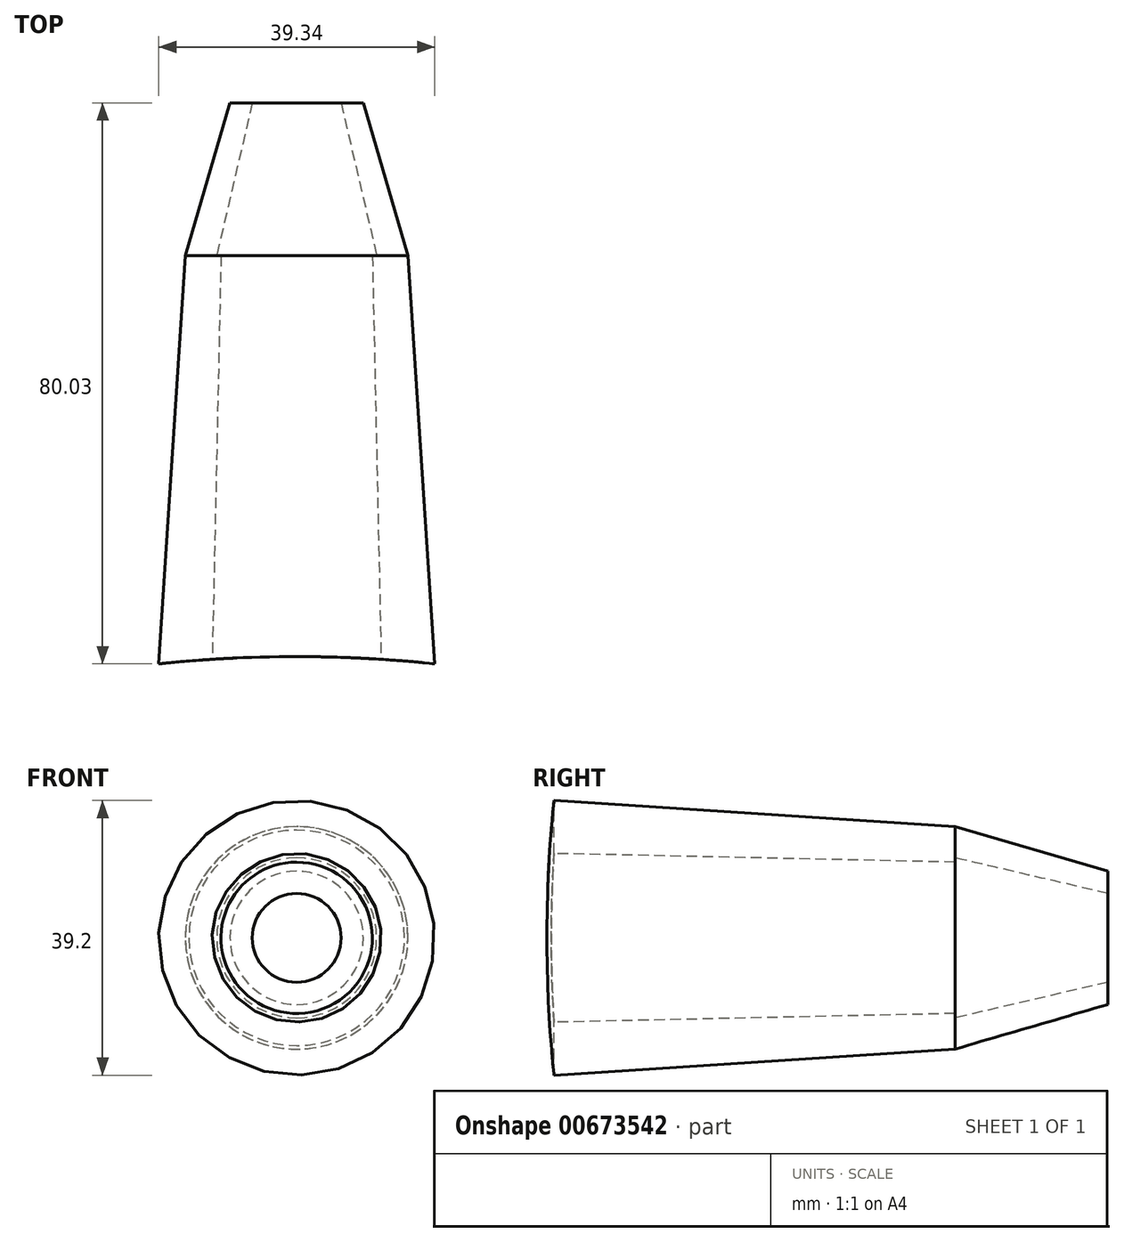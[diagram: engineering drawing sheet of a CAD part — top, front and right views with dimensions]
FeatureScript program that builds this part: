
annotation { "Feature Type Name" : "Feature", "Feature Type Description" : "" }
export const myFeature = defineFeature(function(context is Context, id is Id, definition is map)
    precondition{}
    {
        {
            var Q0;
            Q0=qCreatedBy(makeId("Top.planeOp"),FACE);
            var sketch = newSketch(context, id + "F0", { "sketchPlane" : qUnion([Q0])});
            skLineSegment(sketch, "E0", {"start": v(0, 0) * mm, "end": v(-19.69, 0) * mm});
            skLineSegment(sketch, "E1", {"start": v(-19.69, 0) * mm, "end": v(-15.88, 58.42) * mm});
            skLineSegment(sketch, "E2", {"start": v(-15.88, 58.42) * mm, "end": v(0, 58.42) * mm});
            skLineSegment(sketch, "E3", {"start": v(0, 58.42) * mm, "end": v(0, 0) * mm});
            skLineSegment(sketch, "E4", {"start": v(-10.8, 58.42) * mm, "end": v(-12.06, 0) * mm});
            skSolve(sketch);
        }
        {
            var Q0;
            {var subQ0=sQuery(id+"F0.wireOp",EDGE,"E1");Q0=makeQuery(id+"F0.imprint","IMPRINT",FACE,{"disambiguationData":[TD([[makeQuery(id+"F0.imprint","IMPRINT",EDGE,{"derivedFrom":subQ0}),-1.0]])]});}
            var Q1;
            Q1=sQuery(id+"F0.wireOp",EDGE,"E3");
            revolve(context, id + "F1", {"entities" : qUnion([Q0]), "axis" : qUnion([Q1]), "revolveType" : RevolveType.FULL});
        }
        {
            var Q0;
            Q0=qCreatedBy(makeId("Top.planeOp"),FACE);
            var sketch = newSketch(context, id + "F2", { "sketchPlane" : qUnion([Q0])});
            skCircle(sketch, "E5", {"center": v(0, -187.27) * mm, "radius": 188.5 * mm});
            skSolve(sketch);
        }
        {
            var Q0;
            Q0=makeQuery(id+"F2.imprint","IMPRINT",FACE,{"disambiguationData":[TD([[makeQuery(id+"F2.imprint","IMPRINT",EDGE,{"derivedFrom":sQuery(id+"F2.wireOp",EDGE,"E5")}),1.0]])]});
            extrude(context, id + "F3", {"entities" : qUnion([Q0]), "operationType" : NewBodyOperationType.REMOVE, "endBound" : BoundingType.SYMMETRIC, "oppositeDirection" : true, "depth" : 50.8 * mm, "offsetDistance" : 25.4 * mm});
        }
        {
            var Q0;
            Q0=qCreatedBy(makeId("Top.planeOp"),FACE);
            var sketch = newSketch(context, id + "F4", { "sketchPlane" : qUnion([Q0])});
            skLineSegment(sketch, "E6", {"start": v(-15.88, 58.41) * mm, "end": v(-9.5, 80.23) * mm});
            skLineSegment(sketch, "E7", {"start": v(-9.5, 80.23) * mm, "end": v(0, 80.23) * mm});
            skLineSegment(sketch, "E8", {"start": v(0, 80.23) * mm, "end": v(0, 58.64) * mm});
            skLineSegment(sketch, "E9", {"start": v(0, 58.64) * mm, "end": v(-15.88, 58.41) * mm});
            skLineSegment(sketch, "E10", {"start": v(-11.4, 58.48) * mm, "end": v(-6.33, 80.23) * mm});
            skSolve(sketch);
        }
        {
            var Q0;
            {var subQ0=sQuery(id+"F4.wireOp",EDGE,"E6");Q0=makeQuery(id+"F4.imprint","IMPRINT",FACE,{"disambiguationData":[TD([[makeQuery(id+"F4.imprint","IMPRINT",EDGE,{"derivedFrom":subQ0}),-1.0]])]});}
            var Q1;
            Q1=sQuery(id+"F4.wireOp",EDGE,"E8");
            revolve(context, id + "F5", {"operationType" : NewBodyOperationType.ADD, "entities" : qUnion([Q0]), "axis" : qUnion([Q1]), "revolveType" : RevolveType.FULL});
        }
    });
